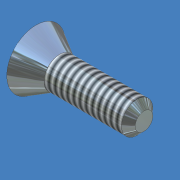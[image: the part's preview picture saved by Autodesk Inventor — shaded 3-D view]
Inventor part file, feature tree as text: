
AUTODESK INVENTOR PART (.ipt)
format: ipt  version: 2011 (Build 150239000, 239)  size: 124,928 bytes
history: native  units: mm (DEFAULTED — no unit token found)
features: sketch x2, revolve x1, chamfer x1, extrude x1, pattern_circular x1, thread x1
ambient origin geometry x8: Origin, YZ Plane, XZ Plane, XY Plane, X Axis, Y Axis, Z Axis, Center Point
bodies: Solid1 (feature_tree)
feature tree (7):
  revolve  "Revolution1"  [1 undecoded]
  chamfer  "Chamfer1"  Distance=1.4605mm
  extrude  "Extrusion1"  TaperAngle=90.0deg  [1 undecoded]
  pattern_circular  "Circular Pattern1"  [2 undecoded]
  thread  "Thread1"  [1 undecoded]
  sketch  "Sketch1"  dims[d0=30.0deg d1=2.7305mm]
  sketch  "Sketch2"  dims[d2=10.0838mm d3=1.4605mm d4=90.0deg d5=0.635mm d6=3.175mm d7=0.6858mm d8=3.048mm d9=1.905mm d10=0.0mm d11=20.0mm d13=90.0deg d14=25.4mm d15=0.0mm d16=45.0deg]
note: 5 required parameter values undecoded (feature->parameter linkage not recoverable at this tier; creation-order binding heuristic only, values carry confidence <= 0.55)